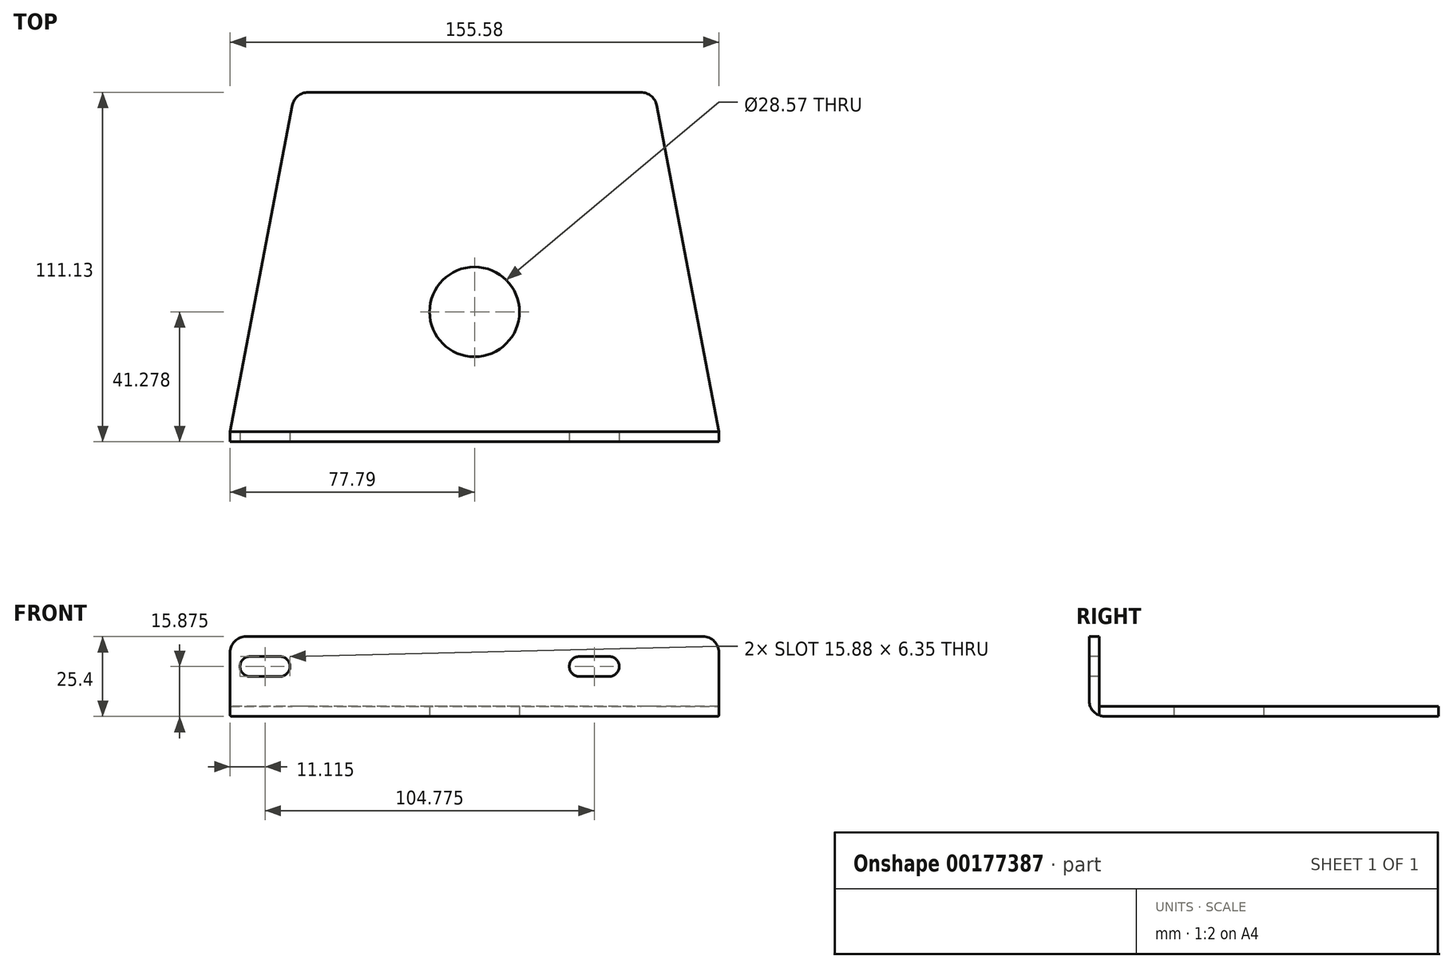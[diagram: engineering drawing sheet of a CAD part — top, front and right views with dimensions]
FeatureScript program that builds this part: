
annotation { "Feature Type Name" : "Feature", "Feature Type Description" : "" }
export const myFeature = defineFeature(function(context is Context, id is Id, definition is map)
    precondition{}
    {
        {
            var Q0;
            Q0=qCreatedBy(makeId("Top.planeOp"),FACE);
            var sketch = newSketch(context, id + "F0", { "sketchPlane" : qUnion([Q0])});
            skLineSegment(sketch, "E0.bottom", {"start": v(77.79, -1.59) * mm, "end": v(-77.79, -1.59) * mm});
            skLineSegment(sketch, "E0.top", {"start": v(77.79, 1.59) * mm, "end": v(-77.79, 1.59) * mm});
            skLineSegment(sketch, "E0.left", {"start": v(77.79, -1.59) * mm, "end": v(77.79, 1.59) * mm});
            skLineSegment(sketch, "E0.right", {"start": v(-77.79, -1.59) * mm, "end": v(-77.79, 1.59) * mm});
            skPoint(sketch, "E0.middle", {"position": v(0, 0) * mm});
            skLineSegment(sketch, "E1", {"start": v(0, 109.54) * mm, "end": v(-57.15, 109.54) * mm});
            skLineSegment(sketch, "E2.MirrorCS", {"start": v(0, 109.54) * mm, "end": v(57.15, 109.54) * mm});
            skLineSegment(sketch, "E3", {"start": v(-77.79, 1.59) * mm, "end": v(-57.15, 109.54) * mm});
            skLineSegment(sketch, "E4", {"start": v(57.15, 109.54) * mm, "end": v(77.79, 1.59) * mm});
            skLineSegment(sketch, "E5", {"start": v(0, 1.59) * mm, "end": v(0, 39.69) * mm});
            skCircle(sketch, "E6", {"center": v(0, 39.69) * mm, "radius": 14.29 * mm});
            skCircle(sketch, "E7.cCircle", {"center": v(0, 39.69) * mm, "radius": 7.14 * mm, "construction": true});
            skSolve(sketch);
        }
        {
            var Q0;
            Q0=makeQuery(id+"F0.imprint","IMPRINT",FACE,{"disambiguationData":[TD([[makeQuery(id+"F0.imprint","IMPRINT",EDGE,{"derivedFrom":sQuery(id+"F0.wireOp",EDGE,"E0.bottom")}),-1.0]])]});
            extrude(context, id + "F1", {"entities" : qUnion([Q0]), "depth" : 25.4 * mm});
        }
        {
            var Q0;
            Q0=makeQuery(id+"F0.imprint","IMPRINT",FACE,{"disambiguationData":[TD([[makeQuery(id+"F0.imprint","IMPRINT",EDGE,{"derivedFrom":sQuery(id+"F0.wireOp",EDGE,"E0.top")}),-1.0]])]});
            var Q1;
            {var subQ0=sQuery(id+"F0.wireOp",EDGE,"E7.4");Q1=makeQuery(id+"F0.imprint","IMPRINT",FACE,{"disambiguationData":[TD([[makeQuery(id+"F0.imprint","IMPRINT",EDGE,{"derivedFrom":subQ0}),1.0]])]});}
            var Q2;
            {var subQ0=sQuery(id+"F0.wireOp",EDGE,"E7.2");Q2=makeQuery(id+"F0.imprint","IMPRINT",FACE,{"disambiguationData":[TD([[makeQuery(id+"F0.imprint","IMPRINT",EDGE,{"derivedFrom":subQ0}),1.0]])]});}
            var Q3;
            {var subQ0=sQuery(id+"F0.wireOp",EDGE,"E7.3");Q3=makeQuery(id+"F0.imprint","IMPRINT",FACE,{"disambiguationData":[TD([[makeQuery(id+"F0.imprint","IMPRINT",EDGE,{"derivedFrom":subQ0}),1.0]])]});}
            var Q4;
            {var subQ0=sQuery(id+"F0.wireOp",EDGE,"E7.5");Q4=makeQuery(id+"F0.imprint","IMPRINT",FACE,{"disambiguationData":[TD([[makeQuery(id+"F0.imprint","IMPRINT",EDGE,{"derivedFrom":subQ0}),1.0]])]});}
            var Q5;
            {var subQ0=sQuery(id+"F0.wireOp",EDGE,"E7.0");Q5=makeQuery(id+"F0.imprint","IMPRINT",FACE,{"disambiguationData":[TD([[makeQuery(id+"F0.imprint","IMPRINT",EDGE,{"derivedFrom":subQ0}),1.0]])]});}
            var Q6;
            {var subQ0=sQuery(id+"F0.wireOp",EDGE,"E7.1");Q6=makeQuery(id+"F0.imprint","IMPRINT",FACE,{"disambiguationData":[TD([[makeQuery(id+"F0.imprint","IMPRINT",EDGE,{"derivedFrom":subQ0}),1.0]])]});}
            extrude(context, id + "F2", {"entities" : qUnion([Q0, Q1, Q2, Q3, Q4, Q5, Q6]), "operationType" : NewBodyOperationType.ADD, "depth" : 3.17 * mm});
        }
        {
            var Q0;
            Q0=makeQuery(id+"F1.opExtrude","CAP_EDGE",EDGE,{"disambiguationData":[OSD([sQuery(id+"F0.wireOp",EDGE,"E0.right")])],"isStart":false});
            var Q1;
            Q1=makeQuery(id+"F1.opExtrude","CAP_EDGE",EDGE,{"disambiguationData":[OSD([sQuery(id+"F0.wireOp",EDGE,"E0.left")])],"isStart":false});
            var Q2;
            Q2=makeQuery(id+"F1.opExtrude","CAP_EDGE",EDGE,{"disambiguationData":[OSD([sQuery(id+"F0.wireOp",EDGE,"E0.bottom")])],"isStart":true});
            var Q3;
            Q3=makeQuery(id+"F2.opExtrude","SWEPT_EDGE",EDGE,{"disambiguationData":[OSD([sQuery(id+"F0.wireOp",EDGE,"E2.MirrorCS"),sQuery(id+"F0.wireOp",EDGE,"E4")])]});
            var Q4;
            Q4=makeQuery(id+"F2.opExtrude","SWEPT_EDGE",EDGE,{"disambiguationData":[OSD([sQuery(id+"F0.wireOp",EDGE,"E1"),sQuery(id+"F0.wireOp",EDGE,"E3")])]});
            fillet(context, id + "F3", {"entities" : qUnion([Q0, Q1, Q2, Q3, Q4]), "radius" : 5.08 * mm, "tangentPropagation" : true, "allowEdgeOverflow" : false});
        }
        {
            var Q0;
            Q0=makeQuery(id+"F1.opExtrude","SWEPT_FACE",FACE,{"disambiguationData":[OSD([sQuery(id+"F0.wireOp",EDGE,"E0.bottom")])]});
            var sketch = newSketch(context, id + "F4", { "sketchPlane" : qUnion([Q0])});
            skLineSegment(sketch, "E8", {"start": v(-77.79, 15.88) * mm, "end": v(-74.61, 15.88) * mm});
            skLineSegment(sketch, "E9", {"start": v(-71.44, 19.05) * mm, "end": v(-61.91, 19.05) * mm});
            skLineSegment(sketch, "E10", {"start": v(-74.61, 15.88) * mm, "end": v(-74.61, 15.88) * mm});
            skLineSegment(sketch, "E11", {"start": v(-71.44, 12.7) * mm, "end": v(-61.91, 12.7) * mm});
            skLineSegment(sketch, "E12", {"start": v(-58.74, 15.88) * mm, "end": v(-58.74, 15.88) * mm});
            skLineSegment(sketch, "E13", {"start": v(49.21, 15.88) * mm, "end": v(46.04, 15.88) * mm});
            skLineSegment(sketch, "E14", {"start": v(46.04, 15.88) * mm, "end": v(46.04, 15.88) * mm});
            skLineSegment(sketch, "E15", {"start": v(42.86, 19.05) * mm, "end": v(33.34, 19.05) * mm});
            skLineSegment(sketch, "E16", {"start": v(30.16, 15.88) * mm, "end": v(30.16, 15.88) * mm});
            skLineSegment(sketch, "E17", {"start": v(33.34, 12.7) * mm, "end": v(42.86, 12.7) * mm});
            skPoint(sketch, "E18.visualSharp", {"position": v(30.16, 19.05) * mm});
            skArc(sketch, "E18.filletArc", {"start": v(33.34, 19.05) * mm, "mid": v(31.1, 18.12) * mm, "end": v(30.16, 15.88) * mm});
            skPoint(sketch, "E19.visualSharp", {"position": v(30.16, 12.7) * mm});
            skArc(sketch, "E19.filletArc", {"start": v(30.16, 15.88) * mm, "mid": v(31.1, 13.63) * mm, "end": v(33.34, 12.7) * mm});
            skPoint(sketch, "E20.visualSharp", {"position": v(46.04, 12.7) * mm});
            skArc(sketch, "E20.filletArc", {"start": v(42.86, 12.7) * mm, "mid": v(45.1, 13.63) * mm, "end": v(46.04, 15.88) * mm});
            skPoint(sketch, "E21.visualSharp", {"position": v(46.04, 19.05) * mm});
            skArc(sketch, "E21.filletArc", {"start": v(46.04, 15.88) * mm, "mid": v(45.1, 18.12) * mm, "end": v(42.86, 19.05) * mm});
            skPoint(sketch, "E22.visualSharp", {"position": v(-58.74, 19.05) * mm});
            skArc(sketch, "E22.filletArc", {"start": v(-58.74, 15.88) * mm, "mid": v(-59.67, 18.12) * mm, "end": v(-61.91, 19.05) * mm});
            skPoint(sketch, "E23.visualSharp", {"position": v(-58.74, 12.7) * mm});
            skArc(sketch, "E23.filletArc", {"start": v(-61.91, 12.7) * mm, "mid": v(-59.67, 13.63) * mm, "end": v(-58.74, 15.88) * mm});
            skPoint(sketch, "E24.visualSharp", {"position": v(-74.61, 12.7) * mm});
            skArc(sketch, "E24.filletArc", {"start": v(-74.61, 15.88) * mm, "mid": v(-73.68, 13.63) * mm, "end": v(-71.44, 12.7) * mm});
            skPoint(sketch, "E25.visualSharp", {"position": v(-74.61, 19.05) * mm});
            skArc(sketch, "E25.filletArc", {"start": v(-71.44, 19.05) * mm, "mid": v(-73.68, 18.12) * mm, "end": v(-74.61, 15.88) * mm});
            skSolve(sketch);
        }
        {
            var Q0;
            Q0=makeQuery(id+"F4.imprint","IMPRINT",FACE,{"disambiguationData":[TD([[makeQuery(id+"F4.imprint","IMPRINT",EDGE,{"derivedFrom":sQuery(id+"F4.wireOp",EDGE,"E9")}),-1.0]])]});
            var Q1;
            Q1=makeQuery(id+"F4.imprint","IMPRINT",FACE,{"disambiguationData":[TD([[makeQuery(id+"F4.imprint","IMPRINT",EDGE,{"derivedFrom":sQuery(id+"F4.wireOp",EDGE,"E15")}),1.0]])]});
            extrude(context, id + "F5", {"entities" : qUnion([Q0, Q1]), "operationType" : NewBodyOperationType.REMOVE, "oppositeDirection" : true, "depth" : 25.4 * mm});
        }
    });
